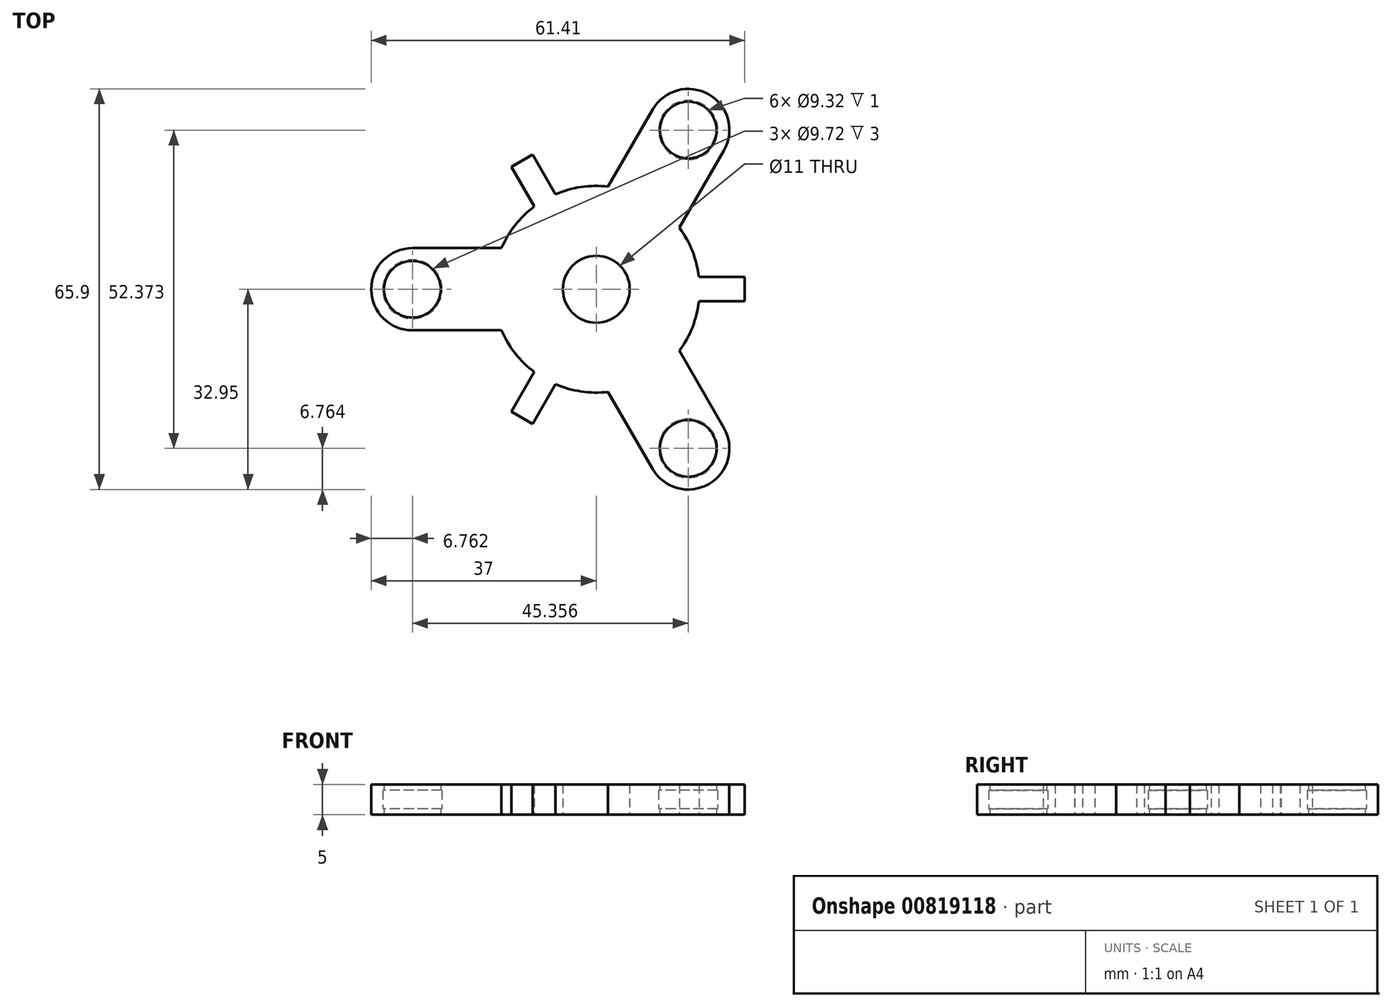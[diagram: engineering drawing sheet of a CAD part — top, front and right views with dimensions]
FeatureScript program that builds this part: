
annotation { "Feature Type Name" : "Feature", "Feature Type Description" : "" }
export const myFeature = defineFeature(function(context is Context, id is Id, definition is map)
    precondition{}
    {
        {
            var Q0;
            Q0=qCreatedBy(makeId("Top.planeOp"),FACE);
            var sketch = newSketch(context, id + "F0", { "sketchPlane" : qUnion([Q0])});
            skCircle(sketch, "E0", {"center": v(0, 0) * mm, "radius": 5.5 * mm});
            skArc(sketch, "E1", {"start": v(16.88, 2) * mm, "mid": v(15.8, 6.27) * mm, "end": v(13.66, 10.13) * mm});
            skPoint(sketch, "E2", {"position": v(24.4, 0) * mm});
            skLineSegment(sketch, "E3", {"start": v(24.4, 0) * mm, "end": v(24.4, 2) * mm});
            skLineSegment(sketch, "E4", {"start": v(24.4, 2) * mm, "end": v(16.88, 2) * mm});
            skLineSegment(sketch, "E5", {"start": v(24.4, -2) * mm, "end": v(16.88, -2) * mm});
            skLineSegment(sketch, "E6", {"start": v(24.4, -2) * mm, "end": v(24.4, 0) * mm});
            skArc(sketch, "E7.trimOffspring", {"start": v(-10.17, 13.62) * mm, "mid": v(-13.33, 10.55) * mm, "end": v(-15.6, 6.76) * mm});
            skArc(sketch, "E8.trimOffspring", {"start": v(-6.7, -15.62) * mm, "mid": v(-2.47, -16.82) * mm, "end": v(1.94, -16.89) * mm});
            skPoint(sketch, "E9", {"position": v(-30.24, 0) * mm});
            skCircle(sketch, "E10", {"center": v(-30.24, 0) * mm, "radius": 6.76 * mm});
            skCircle(sketch, "E11", {"center": v(-30.24, 0) * mm, "radius": 4.66 * mm});
            skLineSegment(sketch, "E12.trimOffspring", {"start": v(-6.7, 15.62) * mm, "end": v(-6.7, 15.62) * mm});
            skPoint(sketch, "E13", {"position": v(-37, 0) * mm});
            skLineSegment(sketch, "E14.1.0", {"start": v(-13.94, 20.14) * mm, "end": v(-10.17, 13.62) * mm});
            skLineSegment(sketch, "E14.1.1", {"start": v(-10.47, 22.14) * mm, "end": v(-6.7, 15.62) * mm});
            skLineSegment(sketch, "E14.1.2", {"start": v(-10.47, 22.14) * mm, "end": v(-12.2, 21.14) * mm});
            skLineSegment(sketch, "E14.1.3", {"start": v(-12.2, 21.14) * mm, "end": v(-13.94, 20.14) * mm});
            skLineSegment(sketch, "E14.2.0", {"start": v(-10.47, -22.14) * mm, "end": v(-6.7, -15.62) * mm});
            skLineSegment(sketch, "E14.2.1", {"start": v(-13.94, -20.14) * mm, "end": v(-10.17, -13.62) * mm});
            skLineSegment(sketch, "E14.2.2", {"start": v(-13.94, -20.14) * mm, "end": v(-12.2, -21.14) * mm});
            skLineSegment(sketch, "E14.2.3", {"start": v(-12.2, -21.14) * mm, "end": v(-10.47, -22.14) * mm});
            skLineSegment(sketch, "E15", {"start": v(-30.24, 6.76) * mm, "end": v(-15.6, 6.76) * mm});
            skLineSegment(sketch, "E16", {"start": v(-30.24, -6.76) * mm, "end": v(-15.6, -6.76) * mm});
            skLineSegment(sketch, "E17.1.0", {"start": v(9.26, -29.57) * mm, "end": v(1.94, -16.89) * mm});
            skCircle(sketch, "E17.1.1", {"center": v(15.12, -26.19) * mm, "radius": 6.76 * mm});
            skCircle(sketch, "E17.1.2", {"center": v(15.12, -26.19) * mm, "radius": 4.66 * mm});
            skLineSegment(sketch, "E17.1.3", {"start": v(20.98, -22.8) * mm, "end": v(13.66, -10.13) * mm});
            skLineSegment(sketch, "E17.2.0", {"start": v(20.98, 22.8) * mm, "end": v(13.66, 10.13) * mm});
            skCircle(sketch, "E17.2.1", {"center": v(15.12, 26.19) * mm, "radius": 6.76 * mm});
            skCircle(sketch, "E17.2.2", {"center": v(15.12, 26.19) * mm, "radius": 4.66 * mm});
            skLineSegment(sketch, "E17.2.3", {"start": v(9.26, 29.57) * mm, "end": v(1.94, 16.89) * mm});
            skArc(sketch, "E18.trimOffspring", {"start": v(1.94, 16.89) * mm, "mid": v(-2.47, 16.82) * mm, "end": v(-6.7, 15.62) * mm});
            skArc(sketch, "E19.trimOffspring", {"start": v(13.66, -10.13) * mm, "mid": v(15.8, -6.27) * mm, "end": v(16.88, -2) * mm});
            skArc(sketch, "E20", {"start": v(-15.6, -6.76) * mm, "mid": v(-13.33, -10.55) * mm, "end": v(-10.17, -13.62) * mm});
            skSolve(sketch);
        }
        {
            var Q0;
            Q0 = qSketchRegion(id + "F0", true);
            extrude(context, id + "F1", {"entities" : qUnion([Q0]), "endBound" : BoundingType.SYMMETRIC, "depth" : 5 * mm, "offsetDistance" : 25 * mm});
        }
        {
            var Q0;
            Q0=qCreatedBy(makeId("Top.planeOp"),FACE);
            var sketch = newSketch(context, id + "F2", { "sketchPlane" : qUnion([Q0])});
            skCircle(sketch, "E21.0", {"center": v(-30.24, 0) * mm, "radius": 4.66 * mm, "construction": true});
            skCircle(sketch, "E21.1", {"center": v(15.12, 26.19) * mm, "radius": 4.66 * mm, "construction": true});
            skCircle(sketch, "E21.2", {"center": v(15.12, -26.19) * mm, "radius": 4.66 * mm, "construction": true});
            skCircle(sketch, "E22", {"center": v(-30.24, 0) * mm, "radius": 4.86 * mm});
            skCircle(sketch, "E23", {"center": v(15.12, 26.19) * mm, "radius": 4.86 * mm});
            skCircle(sketch, "E24", {"center": v(15.12, -26.19) * mm, "radius": 4.86 * mm});
            skSolve(sketch);
        }
        {
            var Q0;
            Q0 = qSketchRegion(id + "F2", true);
            extrude(context, id + "F3", {"entities" : qUnion([Q0]), "operationType" : NewBodyOperationType.REMOVE, "endBound" : BoundingType.SYMMETRIC, "depth" : 3 * mm, "offsetDistance" : 25 * mm});
        }
    });
